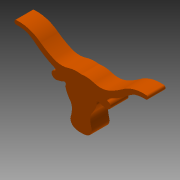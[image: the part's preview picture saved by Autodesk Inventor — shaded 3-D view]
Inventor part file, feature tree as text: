
AUTODESK INVENTOR PART (.ipt)
format: ipt  version: 2014 (Build 180170000, 170)  size: 172,032 bytes
history: native  units: in
note: dims shown in document units (in); Inventor stores cm internally (conversion verified against a paired STEP export)
features: plane x2, extrude x1, sketch x1
ambient origin geometry x8: Origin, YZ Plane, XZ Plane, XY Plane, X Axis, Y Axis, Z Axis, Center Point
bodies: Body1 (feature_tree)
feature tree (4):
  plane  "Work Plane3"
  plane  "Work Plane1"
  extrude  "Extrusion2"  Depth=0.25in TaperAngle=0.0deg
  sketch  "Sketch3"  dims[d8=0.1612in d15=0.25in d16=0.0in]
